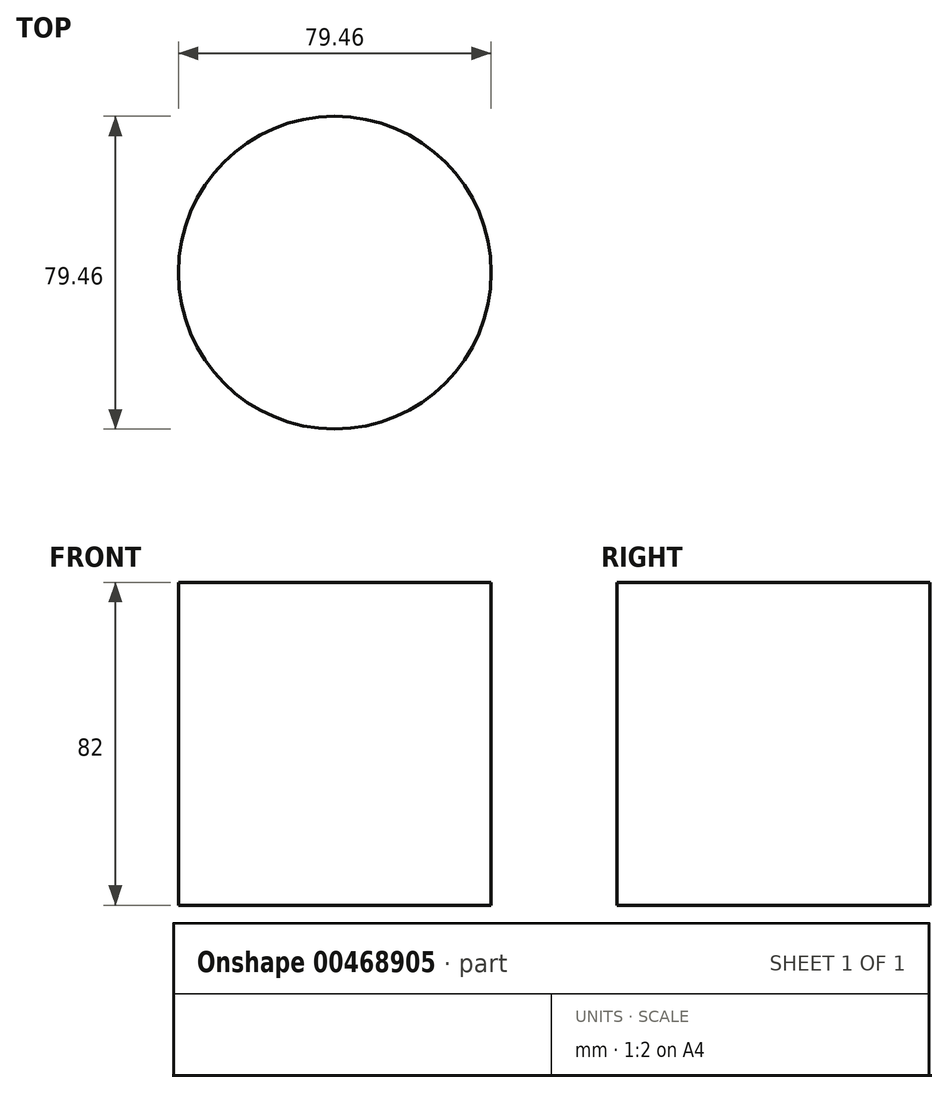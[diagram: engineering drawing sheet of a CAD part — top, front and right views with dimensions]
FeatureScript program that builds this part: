
annotation { "Feature Type Name" : "Feature", "Feature Type Description" : "" }
export const myFeature = defineFeature(function(context is Context, id is Id, definition is map)
    precondition{}
    {
        {
            var Q0;
            Q0=qCreatedBy(makeId("Top.planeOp"),FACE);
            var sketch = newSketch(context, id + "F0", { "sketchPlane" : qUnion([Q0])});
            skCircle(sketch, "E0", {"center": v(0, 0) * mm, "radius": 39.73 * mm});
            skSolve(sketch);
        }
        {
            var Q0;
            Q0 = qSketchRegion(id + "F0", true);
            extrude(context, id + "F1", {"entities" : qUnion([Q0]), "depth" : 82 * mm, "offsetDistance" : 25 * mm});
        }
    });
